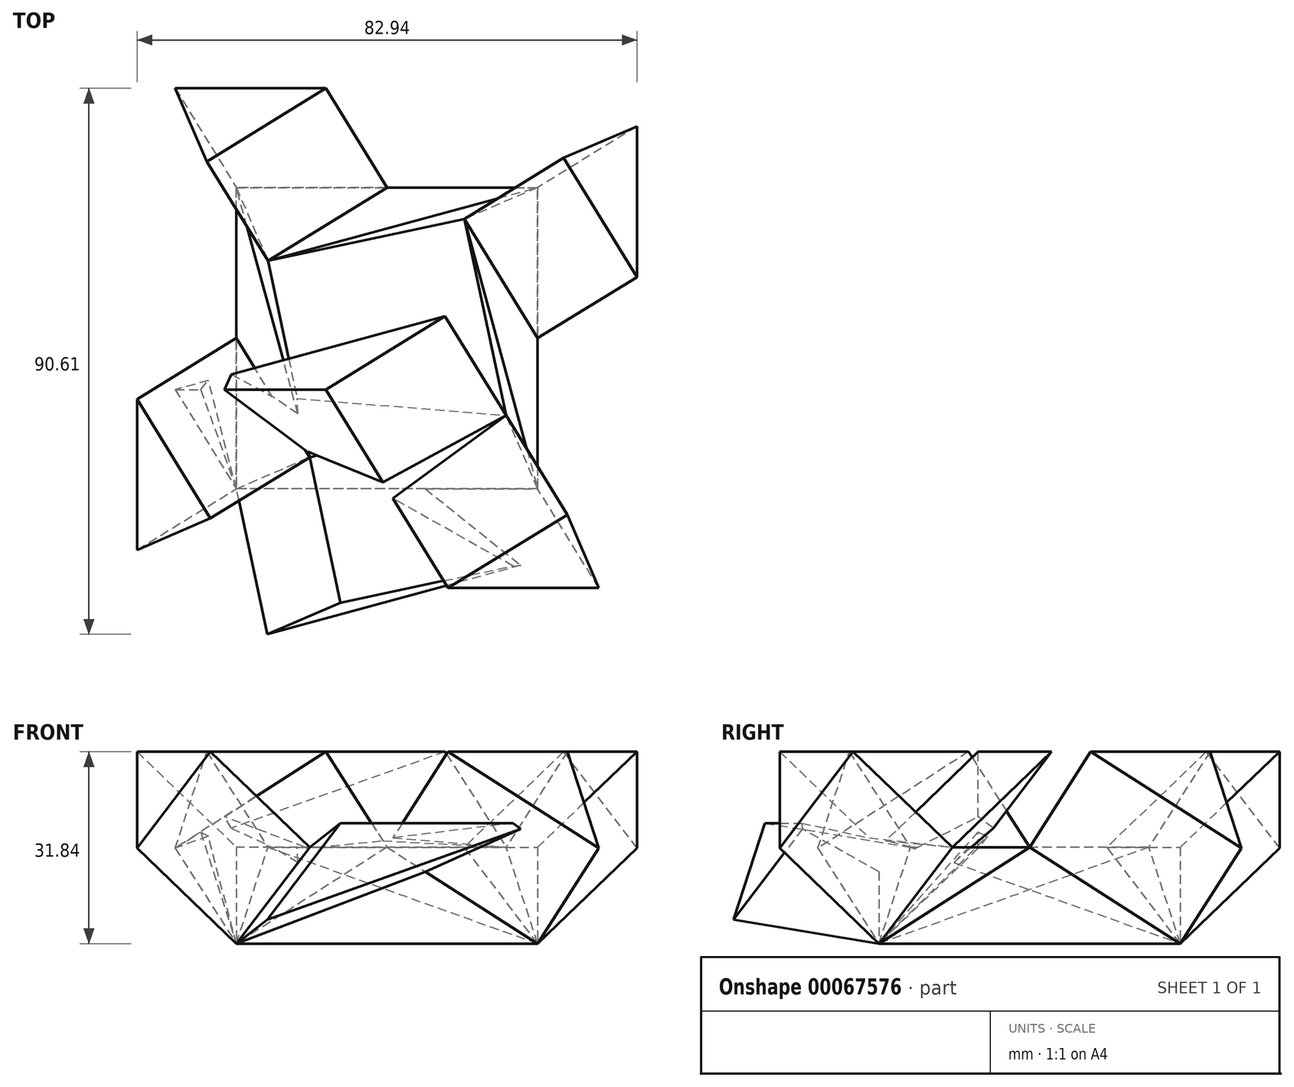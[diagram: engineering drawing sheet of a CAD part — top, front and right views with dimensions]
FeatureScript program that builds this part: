
annotation { "Feature Type Name" : "Feature", "Feature Type Description" : "" }
export const myFeature = defineFeature(function(context is Context, id is Id, definition is map)
    precondition{}
    {
        {
            var Q0;
            Q0=qCreatedBy(makeId("Top.planeOp"),FACE);
            var sketch = newSketch(context, id + "F0", { "sketchPlane" : qUnion([Q0])});
            skLineSegment(sketch, "E0.rect.bottom", {"start": v(25, -25) * mm, "end": v(-25, -25) * mm});
            skLineSegment(sketch, "E0.rect.top", {"start": v(25, 25) * mm, "end": v(-25, 25) * mm});
            skLineSegment(sketch, "E0.rect.left", {"start": v(25, -25) * mm, "end": v(25, 25) * mm});
            skLineSegment(sketch, "E0.rect.right", {"start": v(-25, -25) * mm, "end": v(-25, 25) * mm});
            skPoint(sketch, "E0.rect.middle", {"position": v(0, 0) * mm});
            skSolve(sketch);
        }
        {
            var Q0;
            Q0=qCreatedBy(makeId("Top.planeOp"),FACE);
            cPlane(context, id + "F1", {"entities" : qUnion([Q0]), "cplaneType" : CPlaneType.OFFSET, "offset" : 16 * mm, "width" : 152.4 * mm, "height" : 152.4 * mm});
        }
        {
            var Q0;
            Q0=qCreatedBy(id+"F1.planeOp",FACE);
            var sketch = newSketch(context, id + "F2", { "sketchPlane" : qUnion([Q0])});
            skLineSegment(sketch, "E1.rect.bottom", {"start": v(25, -25) * mm, "end": v(-25, -25) * mm});
            skLineSegment(sketch, "E1.rect.top", {"start": v(25, 25) * mm, "end": v(-25, 25) * mm});
            skLineSegment(sketch, "E1.rect.left", {"start": v(25, -25) * mm, "end": v(25, 25) * mm});
            skLineSegment(sketch, "E1.rect.right", {"start": v(-25, -25) * mm, "end": v(-25, 25) * mm});
            skPoint(sketch, "E1.rect.middle", {"position": v(0, 0) * mm});
            skLineSegment(sketch, "E2", {"start": v(-25, 25) * mm, "end": v(25, -25) * mm});
            skLineSegment(sketch, "E3", {"start": v(-25, -25) * mm, "end": v(25, 25) * mm});
            skLineSegment(sketch, "E4", {"start": v(-25, 16.24) * mm, "end": v(25, -16.24) * mm});
            skLineSegment(sketch, "E5", {"start": v(-16.24, -25) * mm, "end": v(16.24, 25) * mm});
            skLineSegment(sketch, "E6", {"start": v(-19.77, 12.84) * mm, "end": v(-12.84, -19.77) * mm});
            skLineSegment(sketch, "E7", {"start": v(-12.84, -19.77) * mm, "end": v(19.77, -12.84) * mm});
            skLineSegment(sketch, "E8", {"start": v(19.77, -12.84) * mm, "end": v(12.84, 19.77) * mm});
            skLineSegment(sketch, "E9", {"start": v(12.84, 19.77) * mm, "end": v(-19.77, 12.84) * mm});
            skPoint(sketch, "E10", {"position": v(-25, 0) * mm});
            skPoint(sketch, "E11", {"position": v(0, 25) * mm});
            skPoint(sketch, "E12", {"position": v(25, 0) * mm});
            skPoint(sketch, "E13", {"position": v(0, -25) * mm});
            skSolve(sketch);
        }
        {
            var Q0;
            {var subQ0=sQuery(id+"F2.wireOp",EDGE,"E9");var subQ1=sQuery(id+"F2.wireOp",EDGE,"E2");var subQ2=makeQuery(id+"F2.imprint","INTERSECT",VERTEX,{"derivedFrom":[subQ1,subQ0]});Q0=makeQuery(id+"F2.imprint","IMPRINT",FACE,{"disambiguationData":[TD([[makeQuery(id+"F2.imprint","IMPRINT",EDGE,{"disambiguationData":[TD([[subQ2,-1.0]])],"derivedFrom":subQ0}),1.0]])]});}
            var Q1;
            {var subQ0=sQuery(id+"F2.wireOp",EDGE,"E6");var subQ1=sQuery(id+"F2.wireOp",EDGE,"E3");var subQ2=makeQuery(id+"F2.imprint","INTERSECT",VERTEX,{"derivedFrom":[subQ1,subQ0]});Q1=makeQuery(id+"F2.imprint","IMPRINT",FACE,{"disambiguationData":[TD([[makeQuery(id+"F2.imprint","IMPRINT",EDGE,{"disambiguationData":[TD([[subQ2,1.0]])],"derivedFrom":subQ0}),1.0]])]});}
            var Q2;
            {var subQ0=sQuery(id+"F2.wireOp",EDGE,"E9");var subQ1=sQuery(id+"F2.wireOp",EDGE,"E2");var subQ2=makeQuery(id+"F2.imprint","INTERSECT",VERTEX,{"derivedFrom":[subQ1,subQ0]});Q2=makeQuery(id+"F2.imprint","IMPRINT",FACE,{"disambiguationData":[TD([[makeQuery(id+"F2.imprint","IMPRINT",EDGE,{"disambiguationData":[TD([[subQ2,1.0]])],"derivedFrom":subQ0}),1.0]])]});}
            var Q3;
            {var subQ0=sQuery(id+"F2.wireOp",EDGE,"E8");var subQ1=sQuery(id+"F2.wireOp",EDGE,"E3");var subQ2=makeQuery(id+"F2.imprint","INTERSECT",VERTEX,{"derivedFrom":[subQ1,subQ0]});Q3=makeQuery(id+"F2.imprint","IMPRINT",FACE,{"disambiguationData":[TD([[makeQuery(id+"F2.imprint","IMPRINT",EDGE,{"disambiguationData":[TD([[subQ2,-1.0]])],"derivedFrom":subQ0}),1.0]])]});}
            var Q4;
            {var subQ0=sQuery(id+"F2.wireOp",EDGE,"E6");var subQ1=sQuery(id+"F2.wireOp",EDGE,"E3");var subQ2=makeQuery(id+"F2.imprint","INTERSECT",VERTEX,{"derivedFrom":[subQ1,subQ0]});Q4=makeQuery(id+"F2.imprint","IMPRINT",FACE,{"disambiguationData":[TD([[makeQuery(id+"F2.imprint","IMPRINT",EDGE,{"disambiguationData":[TD([[subQ2,-1.0]])],"derivedFrom":subQ0}),1.0]])]});}
            var Q5;
            {var subQ0=sQuery(id+"F2.wireOp",EDGE,"E7");var subQ1=sQuery(id+"F2.wireOp",EDGE,"E2");var subQ2=makeQuery(id+"F2.imprint","INTERSECT",VERTEX,{"derivedFrom":[subQ1,subQ0]});Q5=makeQuery(id+"F2.imprint","IMPRINT",FACE,{"disambiguationData":[TD([[makeQuery(id+"F2.imprint","IMPRINT",EDGE,{"disambiguationData":[TD([[subQ2,1.0]])],"derivedFrom":subQ0}),1.0]])]});}
            var Q6;
            {var subQ0=sQuery(id+"F2.wireOp",EDGE,"E8");var subQ1=sQuery(id+"F2.wireOp",EDGE,"E3");var subQ2=makeQuery(id+"F2.imprint","INTERSECT",VERTEX,{"derivedFrom":[subQ1,subQ0]});Q6=makeQuery(id+"F2.imprint","IMPRINT",FACE,{"disambiguationData":[TD([[makeQuery(id+"F2.imprint","IMPRINT",EDGE,{"disambiguationData":[TD([[subQ2,1.0]])],"derivedFrom":subQ0}),1.0]])]});}
            var Q7;
            {var subQ0=sQuery(id+"F2.wireOp",EDGE,"E7");var subQ1=sQuery(id+"F2.wireOp",EDGE,"E2");var subQ2=makeQuery(id+"F2.imprint","INTERSECT",VERTEX,{"derivedFrom":[subQ1,subQ0]});Q7=makeQuery(id+"F2.imprint","IMPRINT",FACE,{"disambiguationData":[TD([[makeQuery(id+"F2.imprint","IMPRINT",EDGE,{"disambiguationData":[TD([[subQ2,-1.0]])],"derivedFrom":subQ0}),1.0]])]});}
            extrude(context, id + "F3", {"entities" : qUnion([Q0, Q1, Q2, Q3, Q4, Q5, Q6, Q7]), "oppositeDirection" : true, "depth" : 16 * mm});
        }
        {
            var Q0;
            Q0=sQuery(id+"F2.wireOp",VERTEX,"E8.start");
            var Q1;
            Q1=sQuery(id+"F2.wireOp",VERTEX,"E13");
            var Q2;
            Q2=sQuery(id+"F0.wireOp",VERTEX,"E0.rect.left.start");
            cPlane(context, id + "F4", {"entities" : qUnion([Q0, Q1, Q2]), "cplaneType" : CPlaneType.THREE_POINT, "offset" : 150 * mm, "width" : 150 * mm, "height" : 150 * mm});
        }
        {
            var Q0;
            Q0=qCreatedBy(id+"F4.planeOp",FACE);
            var sketch = newSketch(context, id + "F5", { "sketchPlane" : qUnion([Q0])});
            skLineSegment(sketch, "E14", {"start": v(-9.82, 2.64) * mm, "end": v(11.8, -5.8) * mm});
            skLineSegment(sketch, "E15", {"start": v(11.8, -5.8) * mm, "end": v(-15.55, -17.33) * mm});
            skLineSegment(sketch, "E16", {"start": v(-15.55, -17.33) * mm, "end": v(-9.82, 2.64) * mm});
            skSolve(sketch);
        }
        {
            var Q0;
            Q0=makeQuery(id+"F0.imprint","IMPRINT",FACE,{"disambiguationData":[TD([[makeQuery(id+"F0.imprint","IMPRINT",EDGE,{"derivedFrom":sQuery(id+"F0.wireOp",EDGE,"E0.rect.bottom")}),-1.0]])]});
            var sketch = newSketch(context, id + "F6", { "sketchPlane" : qUnion([Q0])});
            skLineSegment(sketch, "E17", {"start": v(0, -25) * mm, "end": v(25, -25) * mm});
            skLineSegment(sketch, "E18", {"start": v(25, -25) * mm, "end": v(19.77, -12.84) * mm});
            skLineSegment(sketch, "E19", {"start": v(19.77, -12.84) * mm, "end": v(0, -25) * mm});
            skSolve(sketch);
        }
        {
            var Q0;
            Q0 = qSketchRegion(id + "F5", true);
            extrude(context, id + "F7", {"entities" : qUnion([Q0]), "oppositeDirection" : true, "depth" : 25 * mm});
        }
        {
            var Q0;
            Q0 = qSketchRegion(id + "F6", true);
            var Q1;
            Q1=makeQuery(id+"F7.opExtrude","SWEPT_BODY",BODY,{"disambiguationData":[OSD([sQuery(id+"F5.wireOp",EDGE,"E14"),sQuery(id+"F5.wireOp",EDGE,"E15"),sQuery(id+"F5.wireOp",EDGE,"E16")])]});
            extrude(context, id + "F8", {"entities" : qUnion([Q0]), "operationType" : NewBodyOperationType.ADD, "endBound" : BoundingType.UP_TO_BODY, "endBoundEntityBody" : qUnion([Q1]), "depth" : 25 * mm});
        }
        {
            var Q0;
            Q0=sQuery(id+"F2.wireOp",VERTEX,"E8.start");
            var Q1;
            Q1=sQuery(id+"F2.wireOp",VERTEX,"E13");
            var Q2;
            Q2=sQuery(id+"F0.wireOp",VERTEX,"E0.rect.right.start");
            cPlane(context, id + "F9", {"entities" : qUnion([Q0, Q1, Q2]), "cplaneType" : CPlaneType.THREE_POINT, "offset" : 150 * mm, "width" : 150 * mm, "height" : 150 * mm});
        }
        {
            var Q0;
            Q0=qCreatedBy(id+"F9.planeOp",FACE);
            var sketch = newSketch(context, id + "F10", { "sketchPlane" : qUnion([Q0])});
            skLineSegment(sketch, "E20", {"start": v(30.16, 17.33) * mm, "end": v(2.81, 28.86) * mm});
            skLineSegment(sketch, "E21", {"start": v(2.81, 28.86) * mm, "end": v(-18.81, 20.43) * mm});
            skLineSegment(sketch, "E22", {"start": v(-18.81, 20.43) * mm, "end": v(30.16, 17.33) * mm});
            skSolve(sketch);
        }
        {
            var Q0;
            Q0=makeQuery(id+"F0.imprint","IMPRINT",FACE,{"disambiguationData":[TD([[makeQuery(id+"F0.imprint","IMPRINT",EDGE,{"derivedFrom":sQuery(id+"F0.wireOp",EDGE,"E0.rect.bottom")}),-1.0]])]});
            var sketch = newSketch(context, id + "F11", { "sketchPlane" : qUnion([Q0])});
            skLineSegment(sketch, "E23", {"start": v(0, -25) * mm, "end": v(19.77, -12.84) * mm});
            skLineSegment(sketch, "E24", {"start": v(19.77, -12.84) * mm, "end": v(-25, -25) * mm});
            skLineSegment(sketch, "E25", {"start": v(-25, -25) * mm, "end": v(0, -25) * mm});
            skSolve(sketch);
        }
        {
            var Q0;
            Q0 = qSketchRegion(id + "F10", true);
            extrude(context, id + "F12", {"entities" : qUnion([Q0]), "depth" : 25 * mm});
        }
        {
            var Q0;
            Q0=makeQuery(id+"F11.imprint","IMPRINT",FACE,{"disambiguationData":[TD([[makeQuery(id+"F11.imprint","IMPRINT",EDGE,{"derivedFrom":sQuery(id+"F11.wireOp",EDGE,"E23")}),1.0]])]});
            var Q1;
            Q1=makeQuery(id+"F12.opExtrude","SWEPT_BODY",BODY,{"disambiguationData":[OSD([sQuery(id+"F10.wireOp",EDGE,"E20"),sQuery(id+"F10.wireOp",EDGE,"E21"),sQuery(id+"F10.wireOp",EDGE,"E22")])]});
            extrude(context, id + "F13", {"entities" : qUnion([Q0]), "endBound" : BoundingType.UP_TO_BODY, "endBoundEntityBody" : qUnion([Q1]), "depth" : 25 * mm});
        }
        {
            var Q0;
            Q0=sQuery(id+"F2.wireOp",VERTEX,"E8.start");
            var Q1;
            Q1=sQuery(id+"F2.wireOp",VERTEX,"E7.start");
            var Q2;
            Q2=sQuery(id+"F0.wireOp",VERTEX,"E0.rect.right.start");
            cPlane(context, id + "F14", {"entities" : qUnion([Q0, Q1, Q2]), "cplaneType" : CPlaneType.THREE_POINT, "offset" : 150 * mm, "width" : 150 * mm, "height" : 150 * mm});
        }
        {
            var Q0;
            Q0=qCreatedBy(id+"F14.planeOp",FACE);
            var sketch = newSketch(context, id + "F15", { "sketchPlane" : qUnion([Q0])});
            skLineSegment(sketch, "E26", {"start": v(29.53, -4.08) * mm, "end": v(17.1, 12.56) * mm});
            skLineSegment(sketch, "E27", {"start": v(17.1, 12.56) * mm, "end": v(-16.21, 13.7) * mm});
            skLineSegment(sketch, "E28", {"start": v(-16.21, 13.7) * mm, "end": v(29.53, -4.08) * mm});
            skSolve(sketch);
        }
        {
            var Q0;
            Q0=makeQuery(id+"F0.imprint","IMPRINT",FACE,{"disambiguationData":[TD([[makeQuery(id+"F0.imprint","IMPRINT",EDGE,{"derivedFrom":sQuery(id+"F0.wireOp",EDGE,"E0.rect.bottom")}),-1.0]])]});
            var sketch = newSketch(context, id + "F16", { "sketchPlane" : qUnion([Q0])});
            skLineSegment(sketch, "E29", {"start": v(-12.84, -19.77) * mm, "end": v(-25, -25) * mm});
            skLineSegment(sketch, "E30", {"start": v(-25, -25) * mm, "end": v(19.77, -12.84) * mm});
            skLineSegment(sketch, "E31", {"start": v(19.77, -12.84) * mm, "end": v(-12.84, -19.77) * mm});
            skSolve(sketch);
        }
        {
            var Q0;
            Q0 = qSketchRegion(id + "F15", true);
            extrude(context, id + "F17", {"entities" : qUnion([Q0]), "oppositeDirection" : true, "depth" : 25 * mm});
        }
        {
            var Q0;
            Q0=makeQuery(id+"F16.imprint","IMPRINT",FACE,{"disambiguationData":[TD([[makeQuery(id+"F16.imprint","IMPRINT",EDGE,{"derivedFrom":sQuery(id+"F16.wireOp",EDGE,"E29")}),1.0]])]});
            var Q1;
            Q1=makeQuery(id+"F17.opExtrude","SWEPT_BODY",BODY,{"disambiguationData":[OSD([sQuery(id+"F15.wireOp",EDGE,"E26"),sQuery(id+"F15.wireOp",EDGE,"E27"),sQuery(id+"F15.wireOp",EDGE,"E28")])]});
            extrude(context, id + "F18", {"entities" : qUnion([Q0]), "endBound" : BoundingType.UP_TO_BODY, "endBoundEntityBody" : qUnion([Q1]), "depth" : 25 * mm});
        }
        {
            var Q0;
            Q0=qCreatedBy(makeId("Front.planeOp"),FACE);
            var sketch = newSketch(context, id + "F19", { "sketchPlane" : qUnion([Q0])});
            skLineSegment(sketch, "E32", {"start": v(0, 0) * mm, "end": v(0, 39.33) * mm});
            skSolve(sketch);
        }
        {
            var Q0;
            Q0=makeQuery(id+"F8.opExtrude","SWEPT_BODY",BODY,{"disambiguationData":[OSD([sQuery(id+"F6.wireOp",EDGE,"E17"),sQuery(id+"F6.wireOp",EDGE,"E18"),sQuery(id+"F6.wireOp",EDGE,"E19")])]});
            var Q1;
            Q1=makeQuery(id+"F13.opExtrude","SWEPT_BODY",BODY,{"disambiguationData":[OSD([sQuery(id+"F11.wireOp",EDGE,"E23"),sQuery(id+"F11.wireOp",EDGE,"E24"),sQuery(id+"F11.wireOp",EDGE,"E25")])]});
            var Q2;
            Q2=makeQuery(id+"F18.opExtrude","SWEPT_BODY",BODY,{"disambiguationData":[OSD([sQuery(id+"F16.wireOp",EDGE,"E29"),sQuery(id+"F16.wireOp",EDGE,"E30"),sQuery(id+"F16.wireOp",EDGE,"E31")])]});
            var Q3;
            Q3=sQuery(id+"F19.wireOp",EDGE,"E32");
            circularPattern(context, id + "F20", {"operationType" : NewBodyOperationType.ADD, "entities" : qUnion([Q0, Q1, Q2]), "axis" : qUnion([Q3]), "angle" : 360 * degree, "instanceCount" : 4, "equalSpace" : true});
        }
    });
